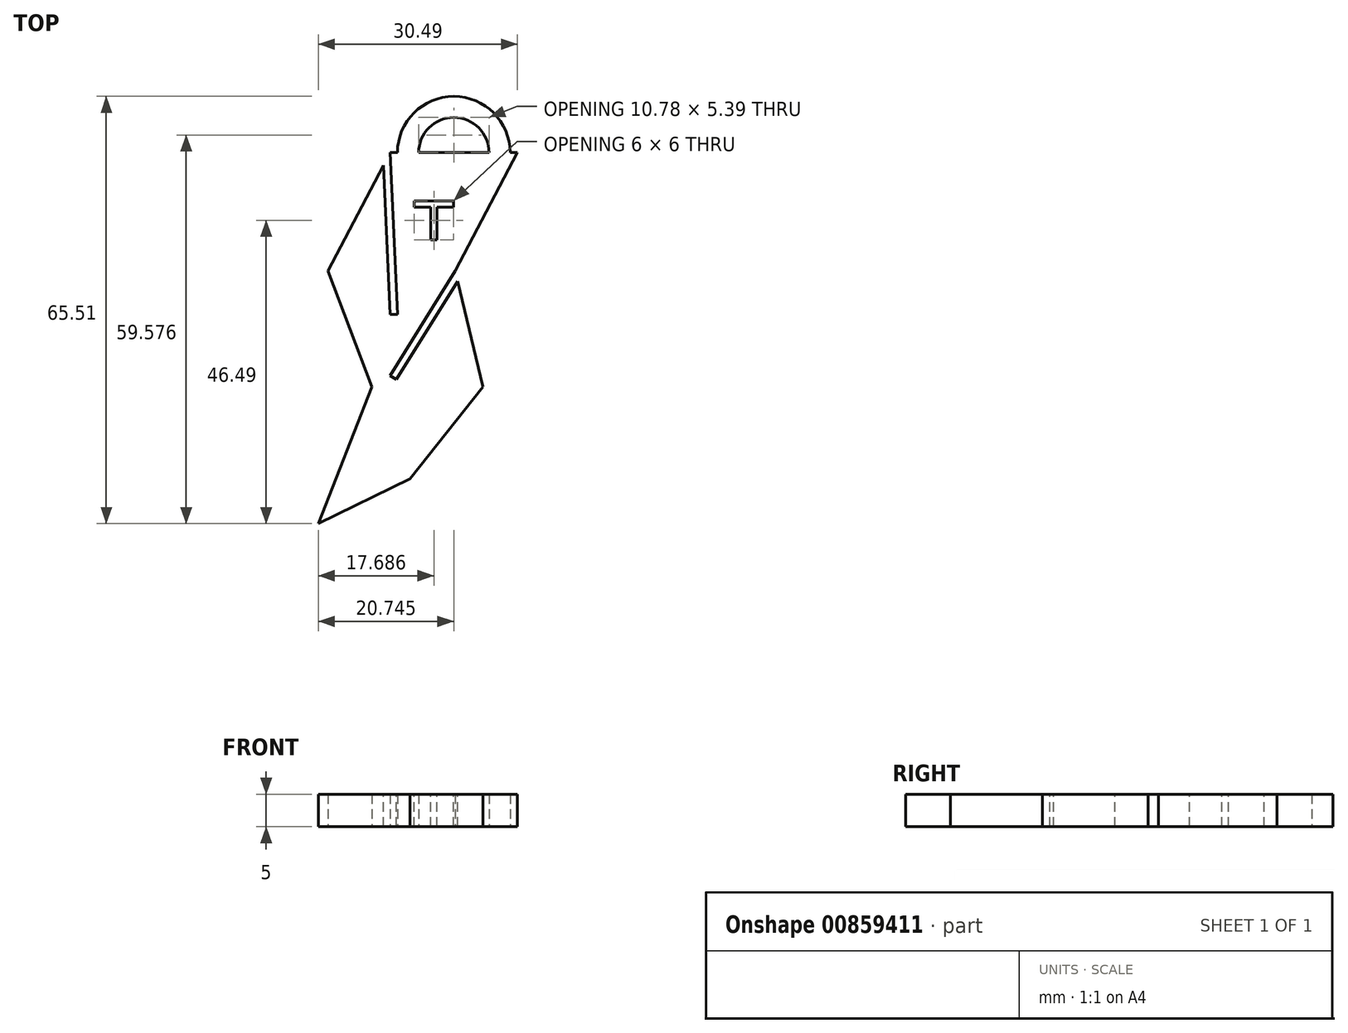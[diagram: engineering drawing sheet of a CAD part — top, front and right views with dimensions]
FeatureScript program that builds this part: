
annotation { "Feature Type Name" : "Feature", "Feature Type Description" : "" }
export const myFeature = defineFeature(function(context is Context, id is Id, definition is map)
    precondition{}
    {
        {
            var Q0;
            Q0=qCreatedBy(makeId("Top.planeOp"),FACE);
            var sketch = newSketch(context, id + "F0", { "sketchPlane" : qUnion([Q0])});
            skLineSegment(sketch, "E0", {"start": v(0, 0) * mm, "end": v(19.5, 0) * mm});
            skLineSegment(sketch, "E1", {"start": v(19.5, 0) * mm, "end": v(9.94, -18.16) * mm});
            skLineSegment(sketch, "E2", {"start": v(9.94, -18.16) * mm, "end": v(14.19, -35.93) * mm});
            skLineSegment(sketch, "E3", {"start": v(14.19, -35.93) * mm, "end": v(3.05, -49.99) * mm});
            skLineSegment(sketch, "E4", {"start": v(0, 0) * mm, "end": v(-9.55, -18.16) * mm});
            skLineSegment(sketch, "E5", {"start": v(-9.55, -18.16) * mm, "end": v(-2.78, -35.93) * mm});
            skLineSegment(sketch, "E6", {"start": v(-2.78, -35.93) * mm, "end": v(-11, -56.88) * mm});
            skLineSegment(sketch, "E7", {"start": v(-11, -56.88) * mm, "end": v(3.05, -49.99) * mm});
            skCircle(sketch, "E8", {"center": v(9.75, 0) * mm, "radius": 8.63 * mm});
            skCircle(sketch, "E9", {"center": v(9.75, 0) * mm, "radius": 5.4 * mm});
            skSolve(sketch);
        }
        {
            var Q0;
            Q0 = qSketchRegion(id + "F0", true);
            var Q1;
            {var subQ0=sQuery(id+"F0.wireOp",EDGE,"E9");var subQ1=sQuery(id+"F0.wireOp",EDGE,"E0");var subQ2=makeQuery(id+"F0.imprint","INTERSECT",VERTEX,{"disambiguationData":[OD(0.0)],"derivedFrom":[subQ1,subQ0]});Q1=makeQuery(id+"F0.imprint","IMPRINT",FACE,{"disambiguationData":[TD([[makeQuery(id+"F0.imprint","IMPRINT",EDGE,{"disambiguationData":[TD([[subQ2,-1.0]])],"derivedFrom":subQ1}),-1.0]])]});}
            extrude(context, id + "F1", {"entities" : qUnion([Q0, Q1]), "depth" : 5 * mm, "offsetDistance" : 25 * mm});
        }
        {
            var Q0;
            Q0=makeQuery(id+"F1.opExtrude","CAP_FACE",FACE,{"disambiguationData":[OSD([sQuery(id+"F0.wireOp",EDGE,"E0"),sQuery(id+"F0.wireOp",EDGE,"E1"),sQuery(id+"F0.wireOp",EDGE,"E2"),sQuery(id+"F0.wireOp",EDGE,"E3"),sQuery(id+"F0.wireOp",EDGE,"E4"),sQuery(id+"F0.wireOp",EDGE,"E5"),sQuery(id+"F0.wireOp",EDGE,"E6"),sQuery(id+"F0.wireOp",EDGE,"E7"),sQuery(id+"F0.wireOp",EDGE,"E8"),sQuery(id+"F0.wireOp",EDGE,"E9")])],"isStart":false});
            var sketch = newSketch(context, id + "F2", { "sketchPlane" : qUnion([Q0])});
            skLineSegment(sketch, "E10", {"start": v(0, 0) * mm, "end": v(1.12, -24.78) * mm});
            skLineSegment(sketch, "E11", {"start": v(1.12, -24.78) * mm, "end": v(0, -24.83) * mm});
            skLineSegment(sketch, "E12", {"start": v(0, -24.83) * mm, "end": v(-1.03, -1.96) * mm});
            skLineSegment(sketch, "E13", {"start": v(9.94, -18.16) * mm, "end": v(0, -34.18) * mm});
            skLineSegment(sketch, "E14", {"start": v(0, -34.18) * mm, "end": v(0.95, -34.77) * mm});
            skLineSegment(sketch, "E15", {"start": v(0.95, -34.77) * mm, "end": v(10.31, -19.7) * mm});
            skSolve(sketch);
        }
        {
            var Q0;
            Q0 = qSketchRegion(id + "F2", true);
            var Q1;
            {var subQ0=sQuery(id+"F2.wireOp",EDGE,"E10");Q1=makeQuery(id+"F2.imprint","IMPRINT",FACE,{"disambiguationData":[TD([[makeQuery(id+"F2.imprint","IMPRINT",EDGE,{"derivedFrom":subQ0}),-1.0]])]});}
            var Q2;
            {var subQ0=sQuery(id+"F2.wireOp",EDGE,"E13");Q2=makeQuery(id+"F2.imprint","IMPRINT",FACE,{"disambiguationData":[TD([[makeQuery(id+"F2.imprint","IMPRINT",EDGE,{"derivedFrom":subQ0}),1.0]])]});}
            extrude(context, id + "F3", {"entities" : qUnion([Q0, Q1, Q2]), "operationType" : NewBodyOperationType.REMOVE, "oppositeDirection" : true, "depth" : 25 * mm, "offsetDistance" : 25 * mm});
        }
        {
            var Q0;
            Q0=makeQuery(id+"F1.opExtrude","CAP_FACE",FACE,{"disambiguationData":[OSD([sQuery(id+"F0.wireOp",EDGE,"E0"),sQuery(id+"F0.wireOp",EDGE,"E1"),sQuery(id+"F0.wireOp",EDGE,"E2"),sQuery(id+"F0.wireOp",EDGE,"E3"),sQuery(id+"F0.wireOp",EDGE,"E4"),sQuery(id+"F0.wireOp",EDGE,"E5"),sQuery(id+"F0.wireOp",EDGE,"E6"),sQuery(id+"F0.wireOp",EDGE,"E7"),sQuery(id+"F0.wireOp",EDGE,"E8"),sQuery(id+"F0.wireOp",EDGE,"E9")])],"isStart":false});
            var sketch = newSketch(context, id + "F4", { "sketchPlane" : qUnion([Q0])});
            skLineSegment(sketch, "E16", {"start": v(6.19, -8.4) * mm, "end": v(6.19, -13.4) * mm});
            skLineSegment(sketch, "E17", {"start": v(6.19, -13.4) * mm, "end": v(7.19, -13.4) * mm});
            skLineSegment(sketch, "E18", {"start": v(7.19, -13.4) * mm, "end": v(7.19, -8.4) * mm});
            skLineSegment(sketch, "E19", {"start": v(6.19, -8.4) * mm, "end": v(3.69, -8.4) * mm});
            skLineSegment(sketch, "E20", {"start": v(3.69, -8.4) * mm, "end": v(3.69, -7.4) * mm});
            skLineSegment(sketch, "E21", {"start": v(3.69, -7.4) * mm, "end": v(9, -7.4) * mm});
            skLineSegment(sketch, "E22", {"start": v(9, -7.4) * mm, "end": v(9.69, -7.4) * mm});
            skLineSegment(sketch, "E23", {"start": v(9.69, -7.4) * mm, "end": v(9.69, -8.4) * mm});
            skLineSegment(sketch, "E24", {"start": v(9.69, -8.4) * mm, "end": v(7.19, -8.4) * mm});
            skSolve(sketch);
        }
        {
            var Q0;
            Q0 = qSketchRegion(id + "F4", true);
            extrude(context, id + "F5", {"entities" : qUnion([Q0]), "operationType" : NewBodyOperationType.REMOVE, "oppositeDirection" : true, "depth" : 25 * mm, "offsetDistance" : 25 * mm});
        }
    });
